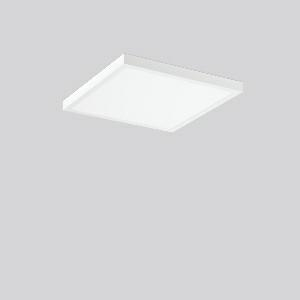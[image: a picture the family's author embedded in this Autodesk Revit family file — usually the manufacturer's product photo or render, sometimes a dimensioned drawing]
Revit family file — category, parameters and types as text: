
# Revit family: sidelite_eco_312376_002_790_7aa2
name_source: partatom
category: Lighting Fixtures
units: mm (PartAtom-declared; Revit-internal decimal feet)

## family parameters
Cut with Voids When Loaded = No
Host = Face
Light Source = No
Part Type = Normal
Room Calculation Point = No
Round Connector Dimension = Use Diameter
Shared = No

## types (1)
- MultiLumen 1 (1 x LED Modul 830, 3400 lm, 3000)
    Apparent Load = 29 VA
    CIE Flux Codes = 46 79 96 100 100
    Color Rendering = 80
    Color Temperature = 3000
    Default Elevation = 1800 mm
    Description = Series: SIDELITE ECO
Highly economical surface mounted luminaire with progressive LED technology. Luminaire frame: aluminium, powder-coated. Mounting frame: sheet steel, powder-coated. Diffuser: plastic, opal. Lightguide and diffuser made of non-yellowing plastic (PMMA). Lateral light emission (RZB SIDELITE technology) for homogeneous light distribution. Driver integrated. MultiLumen: 4 steps adjustable luminous flux. Factory setting is the lowest offered step. Qualified for use in the food and drink industry. 
Colour: white
Length: 602 mm
Width: 602 mm
Height: 47 mm
Lamp: LED
Socket: without socket
Colour temperature: 3000K
Colour rendering index (CRI): 80
System power: 29 W
Rated luminous flux: 3400 lm
Luminous efficiency: 117 lm/W
System power 2: 33 W
Rated luminous flux 2: 3750 lm
Luminous efficiency 2: 114 lm/W
System power 3: 35 W
Rated luminous flux 3: 3950 lm
Luminous efficiency 3: 113 lm/W
System power 4: 38 W
Rated luminous flux 4: 4300 lm
Luminous efficiency 4: 113 lm/W
Control gear: Regulated power supply
Protection class: II
Type of protection: IP 40
    Height = 47 mm
    Lamp = 1 x LED Modul 830
    Lamp Light Flux = 3400 lm
    Lamp count = 1
    Length = 602 mm
    Lifetime = 50000 h
    Luminous efficacy = 117 lm/W
    Manufacturer = RZB
    ModVariant = No
    Model = 312376.002.790
    Mounting Place = Ceiling
    Mounting Type = Surface mounted
    Number of Poles = 1
    OnlyDefault = Yes
    Power Factor = 1
    Product Name = SIDELITE ECO
    Product group = Surface mounted modular luminaires
    ProductGroupID = 306
    Protection Class = Protection class II
    Protection Degree = IP 40
    RLX_Detail_Level = 1
    RLX_Emergency_Light_Flux = 0 lm
    RLX_Emergency_Type = 0
    RLX_Emergency_Type_DB = No
    RlxData = <blob elided: 20289 chars, md5=e5898e1f>
    Socket = socket
    Standby Power = 0 W
    System Light Flux = 3400 lm
    System Power = 29 W
    Type Comments = MultiLumen 1
    Type Image = 312376.002.jpg
    URL = http://relux.com
    VarID = multilumen_1
    Voltage = 230 V
    Voltage Range = 220-240 V
    Weight = 0.00 kg
    Width = 602 mm

## geometry (parser evidence)
native form markers: Blend x4, Sweep x10
no freeform markers — native parametric forms only
